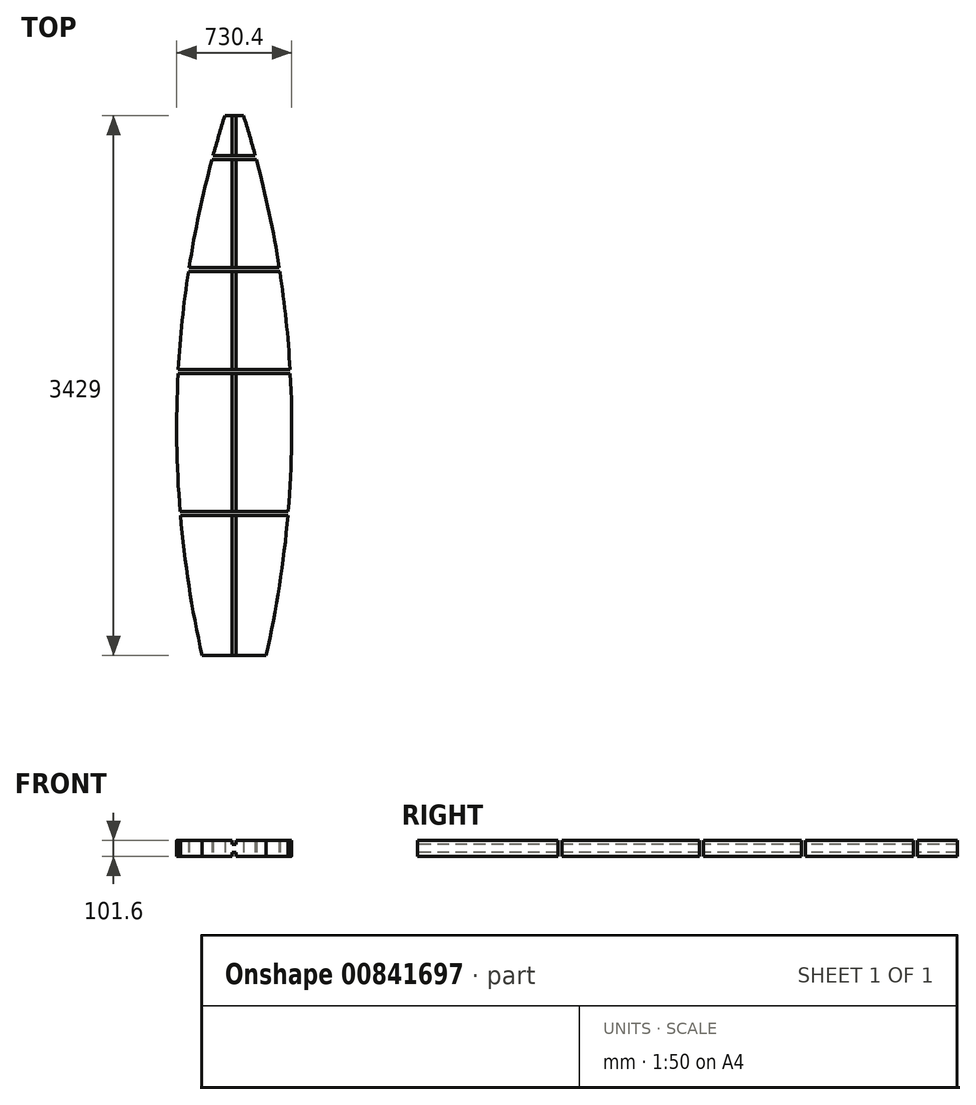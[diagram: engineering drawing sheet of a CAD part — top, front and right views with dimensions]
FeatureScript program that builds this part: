
annotation { "Feature Type Name" : "Feature", "Feature Type Description" : "" }
export const myFeature = defineFeature(function(context is Context, id is Id, definition is map)
    precondition{}
    {
        {
            var Q0;
            Q0=qCreatedBy(makeId("Top.planeOp"),FACE);
            var sketch = newSketch(context, id + "F0", { "sketchPlane" : qUnion([Q0])});
            skLineSegment(sketch, "E0", {"start": v(0, 1803.4) * mm, "end": v(0, -1803.4) * mm, "construction": true});
            skLineSegment(sketch, "E1", {"start": v(0, 0) * mm, "end": v(-355.6, 0) * mm, "construction": true});
            skLineSegment(sketch, "E2", {"start": v(0, -1803.4) * mm, "end": v(-203.2, -1803.4) * mm});
            skArc(sketch, "E3", {"start": v(-59.12, 1625.6) * mm, "mid": v(-97.81, 1498.98) * mm, "end": v(-133.95, 1371.6) * mm});
            skLineSegment(sketch, "E4", {"start": v(0, 1625.6) * mm, "end": v(-59.12, 1625.6) * mm});
            skLineSegment(sketch, "E5", {"start": v(-354.9, 12.7) * mm, "end": v(0, 12.7) * mm});
            skLineSegment(sketch, "E6", {"start": v(-356.28, -12.7) * mm, "end": v(0, -12.7) * mm});
            skLineSegment(sketch, "E7", {"start": v(-133.95, 1371.6) * mm, "end": v(0, 1371.6) * mm});
            skLineSegment(sketch, "E8", {"start": v(-140.82, 1346.2) * mm, "end": v(0, 1346.2) * mm});
            skLineSegment(sketch, "E9", {"start": v(-286.17, 660.4) * mm, "end": v(0, 660.4) * mm});
            skLineSegment(sketch, "E10", {"start": v(-290.1, 635) * mm, "end": v(0, 635) * mm});
            skLineSegment(sketch, "E11", {"start": v(-343.47, -888.07) * mm, "end": v(0, -888.07) * mm});
            skLineSegment(sketch, "E12", {"start": v(-341.35, -913.47) * mm, "end": v(0, -913.47) * mm});
            skArc(sketch, "E13.trimOffspring", {"start": v(-140.82, 1346.2) * mm, "mid": v(-222.67, 1005.24) * mm, "end": v(-286.17, 660.4) * mm});
            skArc(sketch, "E14.trimOffspring", {"start": v(-290.1, 635) * mm, "mid": v(-329.93, 324.62) * mm, "end": v(-354.9, 12.7) * mm});
            skArc(sketch, "E15.trimOffspring", {"start": v(-356.28, -12.7) * mm, "mid": v(-364.5, -450.6) * mm, "end": v(-343.47, -888.07) * mm});
            skArc(sketch, "E16.trimOffspring", {"start": v(-341.35, -913.47) * mm, "mid": v(-287.57, -1360.8) * mm, "end": v(-203.2, -1803.4) * mm});
            skLineSegment(sketch, "E17.MirrorCS", {"start": v(0, 1625.6) * mm, "end": v(59.12, 1625.6) * mm});
            skArc(sketch, "E18.MirrorCS", {"start": v(59.12, 1625.6) * mm, "mid": v(97.81, 1498.98) * mm, "end": v(133.95, 1371.6) * mm});
            skLineSegment(sketch, "E19.MirrorCS", {"start": v(133.95, 1371.6) * mm, "end": v(0, 1371.6) * mm});
            skLineSegment(sketch, "E20.MirrorCS", {"start": v(140.82, 1346.2) * mm, "end": v(0, 1346.2) * mm});
            skArc(sketch, "E21.MirrorCS", {"start": v(140.82, 1346.2) * mm, "mid": v(222.67, 1005.24) * mm, "end": v(286.17, 660.4) * mm});
            skLineSegment(sketch, "E22.MirrorCS", {"start": v(286.17, 660.4) * mm, "end": v(0, 660.4) * mm});
            skLineSegment(sketch, "E23.MirrorCS", {"start": v(290.1, 635) * mm, "end": v(0, 635) * mm});
            skArc(sketch, "E24.MirrorCS", {"start": v(290.1, 635) * mm, "mid": v(329.93, 324.62) * mm, "end": v(354.9, 12.7) * mm});
            skLineSegment(sketch, "E25.MirrorCS", {"start": v(354.9, 12.7) * mm, "end": v(0, 12.7) * mm});
            skLineSegment(sketch, "E26.MirrorCS", {"start": v(356.28, -12.7) * mm, "end": v(0, -12.7) * mm});
            skArc(sketch, "E27.MirrorCS", {"start": v(356.28, -12.7) * mm, "mid": v(364.5, -450.6) * mm, "end": v(343.47, -888.07) * mm});
            skLineSegment(sketch, "E28.MirrorCS", {"start": v(343.47, -888.07) * mm, "end": v(0, -888.07) * mm});
            skLineSegment(sketch, "E29.MirrorCS", {"start": v(341.35, -913.47) * mm, "end": v(0, -913.47) * mm});
            skArc(sketch, "E30.MirrorCS", {"start": v(341.35, -913.47) * mm, "mid": v(287.57, -1360.8) * mm, "end": v(203.2, -1803.4) * mm});
            skLineSegment(sketch, "E31.MirrorCS", {"start": v(0, -1803.4) * mm, "end": v(203.2, -1803.4) * mm});
            skSolve(sketch);
        }
        {
            var Q0;
            Q0 = qSketchRegion(id + "F0", true);
            extrude(context, id + "F1", {"entities" : qUnion([Q0]), "depth" : 101.6 * mm, "offsetDistance" : 25.4 * mm});
        }
        {
            var Q0;
            Q0=makeQuery(id+"F1.opExtrude","SWEPT_FACE",FACE,{"disambiguationData":[OSD([sQuery(id+"F0.wireOp",EDGE,"E2"),sQuery(id+"F0.wireOp",EDGE,"E31.MirrorCS")])]});
            var sketch = newSketch(context, id + "F2", { "sketchPlane" : qUnion([Q0])});
            skLineSegment(sketch, "E32", {"start": v(0, 0) * mm, "end": v(0, 101.6) * mm, "construction": true});
            skLineSegment(sketch, "E33.bottom", {"start": v(-12.7, 101.6) * mm, "end": v(12.7, 101.6) * mm});
            skLineSegment(sketch, "E33.top", {"start": v(-12.7, 76.2) * mm, "end": v(12.7, 76.2) * mm});
            skLineSegment(sketch, "E33.left", {"start": v(-12.7, 101.6) * mm, "end": v(-12.7, 76.2) * mm});
            skLineSegment(sketch, "E33.right", {"start": v(12.7, 101.6) * mm, "end": v(12.7, 76.2) * mm});
            skLineSegment(sketch, "E34.bottom", {"start": v(-12.7, 0) * mm, "end": v(12.7, 0) * mm});
            skLineSegment(sketch, "E34.top", {"start": v(-12.7, 25.4) * mm, "end": v(12.7, 25.4) * mm});
            skLineSegment(sketch, "E34.left", {"start": v(-12.7, 0) * mm, "end": v(-12.7, 25.4) * mm});
            skLineSegment(sketch, "E34.right", {"start": v(12.7, 0) * mm, "end": v(12.7, 25.4) * mm});
            skSolve(sketch);
        }
        {
            var Q0;
            Q0 = qSketchRegion(id + "F2", true);
            extrude(context, id + "F3", {"entities" : qUnion([Q0]), "operationType" : NewBodyOperationType.REMOVE, "oppositeDirection" : true, "depth" : 3657.6 * mm, "offsetDistance" : 25.4 * mm});
        }
    });
